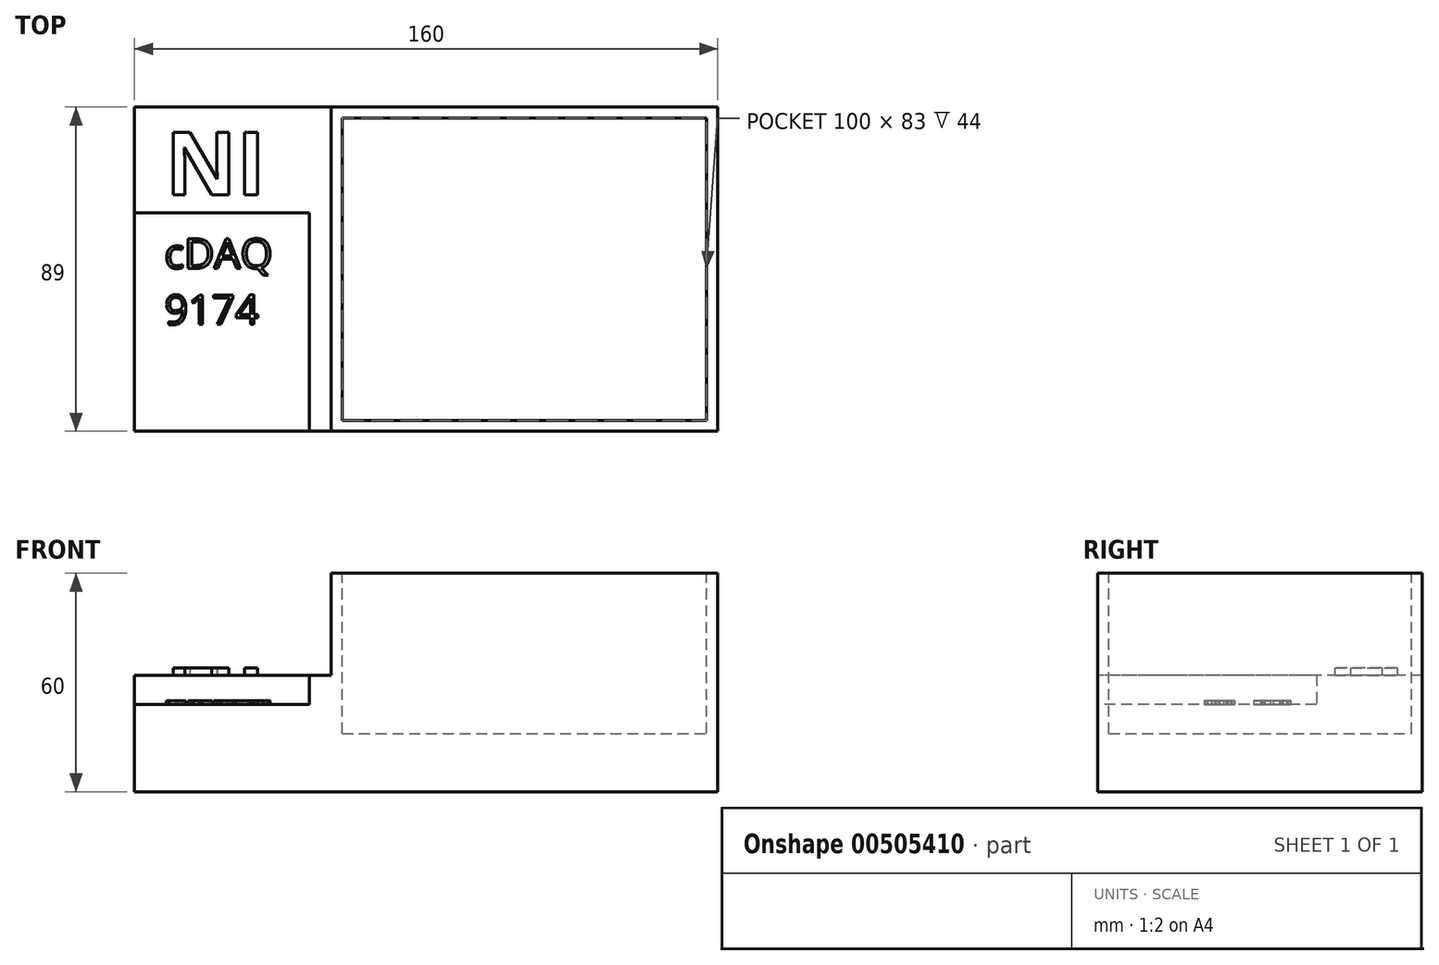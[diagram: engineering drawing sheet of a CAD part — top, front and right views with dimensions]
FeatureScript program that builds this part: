
annotation { "Feature Type Name" : "Feature", "Feature Type Description" : "" }
export const myFeature = defineFeature(function(context is Context, id is Id, definition is map)
    precondition{}
    {
        {
            var Q0;
            Q0=qCreatedBy(makeId("Top.planeOp"),FACE);
            var sketch = newSketch(context, id + "F0", { "sketchPlane" : qUnion([Q0])});
            skLineSegment(sketch, "E0.bottom", {"start": v(0, 0) * mm, "end": v(160, 0) * mm});
            skLineSegment(sketch, "E0.top", {"start": v(0, 89) * mm, "end": v(160, 89) * mm});
            skLineSegment(sketch, "E0.left", {"start": v(0, 0) * mm, "end": v(0, 89) * mm});
            skLineSegment(sketch, "E0.right", {"start": v(160, 0) * mm, "end": v(160, 89) * mm});
            skSolve(sketch);
        }
        {
            var Q0;
            Q0=makeQuery(id+"F0.imprint","IMPRINT",FACE,{"disambiguationData":[TD([[makeQuery(id+"F0.imprint","IMPRINT",EDGE,{"derivedFrom":sQuery(id+"F0.wireOp",EDGE,"E0.bottom")}),1.0]])]});
            extrude(context, id + "F1", {"entities" : qUnion([Q0]), "depth" : 60 * mm});
        }
        {
            var Q0;
            Q0=makeQuery(id+"F1.opExtrude","SWEPT_FACE",FACE,{"disambiguationData":[OSD([sQuery(id+"F0.wireOp",EDGE,"E0.bottom")])]});
            var sketch = newSketch(context, id + "F2", { "sketchPlane" : qUnion([Q0])});
            skLineSegment(sketch, "E1.bottom", {"start": v(0, 60) * mm, "end": v(54, 60) * mm});
            skLineSegment(sketch, "E1.top", {"start": v(0, 32) * mm, "end": v(54, 32) * mm});
            skLineSegment(sketch, "E1.left", {"start": v(0, 60) * mm, "end": v(0, 32) * mm});
            skLineSegment(sketch, "E1.right", {"start": v(54, 60) * mm, "end": v(54, 32) * mm});
            skSolve(sketch);
        }
        {
            var Q0;
            Q0=makeQuery(id+"F2.imprint","IMPRINT",FACE,{"disambiguationData":[TD([[makeQuery(id+"F2.imprint","IMPRINT",EDGE,{"derivedFrom":sQuery(id+"F2.wireOp",EDGE,"E1.bottom")}),-1.0]])]});
            extrude(context, id + "F3", {"entities" : qUnion([Q0]), "operationType" : NewBodyOperationType.REMOVE, "endBound" : BoundingType.THROUGH_ALL, "oppositeDirection" : true, "depth" : 25 * mm});
        }
        {
            var Q0;
            Q0=makeQuery(id+"F1.opExtrude","SWEPT_FACE",FACE,{"disambiguationData":[OSD([sQuery(id+"F0.wireOp",EDGE,"E0.bottom")])]});
            var sketch = newSketch(context, id + "F4", { "sketchPlane" : qUnion([Q0])});
            skLineSegment(sketch, "E2.bottom", {"start": v(0, 32) * mm, "end": v(48, 32) * mm});
            skLineSegment(sketch, "E2.top", {"start": v(0, 24) * mm, "end": v(48, 24) * mm});
            skLineSegment(sketch, "E2.left", {"start": v(0, 32) * mm, "end": v(0, 24) * mm});
            skLineSegment(sketch, "E2.right", {"start": v(48, 32) * mm, "end": v(48, 24) * mm});
            skSolve(sketch);
        }
        {
            var Q0;
            Q0=makeQuery(id+"F4.imprint","IMPRINT",FACE,{"disambiguationData":[TD([[makeQuery(id+"F4.imprint","IMPRINT",EDGE,{"derivedFrom":sQuery(id+"F4.wireOp",EDGE,"E2.bottom")}),-1.0]])]});
            extrude(context, id + "F5", {"entities" : qUnion([Q0]), "operationType" : NewBodyOperationType.REMOVE, "oppositeDirection" : true, "depth" : 60 * mm});
        }
        {
            var Q0;
            Q0=makeQuery(id+"F1.opExtrude","CAP_FACE",FACE,{"disambiguationData":[OSD([sQuery(id+"F0.wireOp",EDGE,"E0.bottom"),sQuery(id+"F0.wireOp",EDGE,"E0.top"),sQuery(id+"F0.wireOp",EDGE,"E0.left"),sQuery(id+"F0.wireOp",EDGE,"E0.right")])],"isStart":false});
            var sketch = newSketch(context, id + "F6", { "sketchPlane" : qUnion([Q0])});
            skLineSegment(sketch, "E3", {"start": v(57, 44.5) * mm, "end": v(57, 86) * mm});
            skLineSegment(sketch, "E4", {"start": v(107, 86) * mm, "end": v(57, 86) * mm});
            skLineSegment(sketch, "E5", {"start": v(157, 44.5) * mm, "end": v(157, 86) * mm});
            skLineSegment(sketch, "E6", {"start": v(107, 86) * mm, "end": v(157, 86) * mm});
            skLineSegment(sketch, "E7", {"start": v(107, 3) * mm, "end": v(157, 3) * mm});
            skLineSegment(sketch, "E8", {"start": v(157, 44.5) * mm, "end": v(157, 3) * mm});
            skLineSegment(sketch, "E9", {"start": v(107, 3) * mm, "end": v(57, 3) * mm});
            skLineSegment(sketch, "E10", {"start": v(57, 44.5) * mm, "end": v(57, 3) * mm});
            skSolve(sketch);
        }
        {
            var Q0;
            Q0=makeQuery(id+"F6.imprint","IMPRINT",FACE,{"disambiguationData":[TD([[makeQuery(id+"F6.imprint","IMPRINT",EDGE,{"derivedFrom":sQuery(id+"F6.wireOp",EDGE,"E3")}),-1.0]])]});
            extrude(context, id + "F7", {"entities" : qUnion([Q0]), "operationType" : NewBodyOperationType.REMOVE, "oppositeDirection" : true, "depth" : 44 * mm});
        }
        {
            var Q0;
            Q0=makeQuery(id+"F3.boolean.opBoolean","COPY",FACE,{"derivedFrom":makeQuery(id+"F3.opExtrude","SWEPT_FACE",FACE,{"disambiguationData":[OSD([sQuery(id+"F2.wireOp",EDGE,"E1.top")])]})});
            var sketch = newSketch(context, id + "F8", { "sketchPlane" : qUnion([Q0])});
            skText(sketch, "E11", { "text": "NI", "fontName": "OpenSans-Bold.ttf"});
            const initialGuessF8  = {"E11": [0.00843, 0.06492, 1, 0, 0.01734]};
            skSetInitialGuess(sketch, initialGuessF8);
            skSolve(sketch);
        }
        {
            var Q0;
            Q0 = qSketchRegion(id + "F8", true);
            extrude(context, id + "F9", {"entities" : qUnion([Q0]), "operationType" : NewBodyOperationType.ADD, "depth" : 2 * mm});
        }
        {
            var Q0;
            Q0=makeQuery(id+"F5.boolean.opBoolean","COPY",FACE,{"derivedFrom":makeQuery(id+"F5.opExtrude","SWEPT_FACE",FACE,{"disambiguationData":[OSD([sQuery(id+"F4.wireOp",EDGE,"E2.top")])]})});
            var sketch = newSketch(context, id + "F10", { "sketchPlane" : qUnion([Q0])});
            skText(sketch, "E12", { "text": "cDAQ\n9174", "fontName": "OpenSans-Regular.ttf"});
            const initialGuessF10  = {"E12": [0.00822, 0.04473, 1, 0, 0.00816]};
            skSetInitialGuess(sketch, initialGuessF10);
            skSolve(sketch);
        }
        {
            var Q0;
            Q0 = qSketchRegion(id + "F10", true);
            extrude(context, id + "F11", {"entities" : qUnion([Q0]), "operationType" : NewBodyOperationType.ADD, "depth" : 1 * mm});
        }
    });
